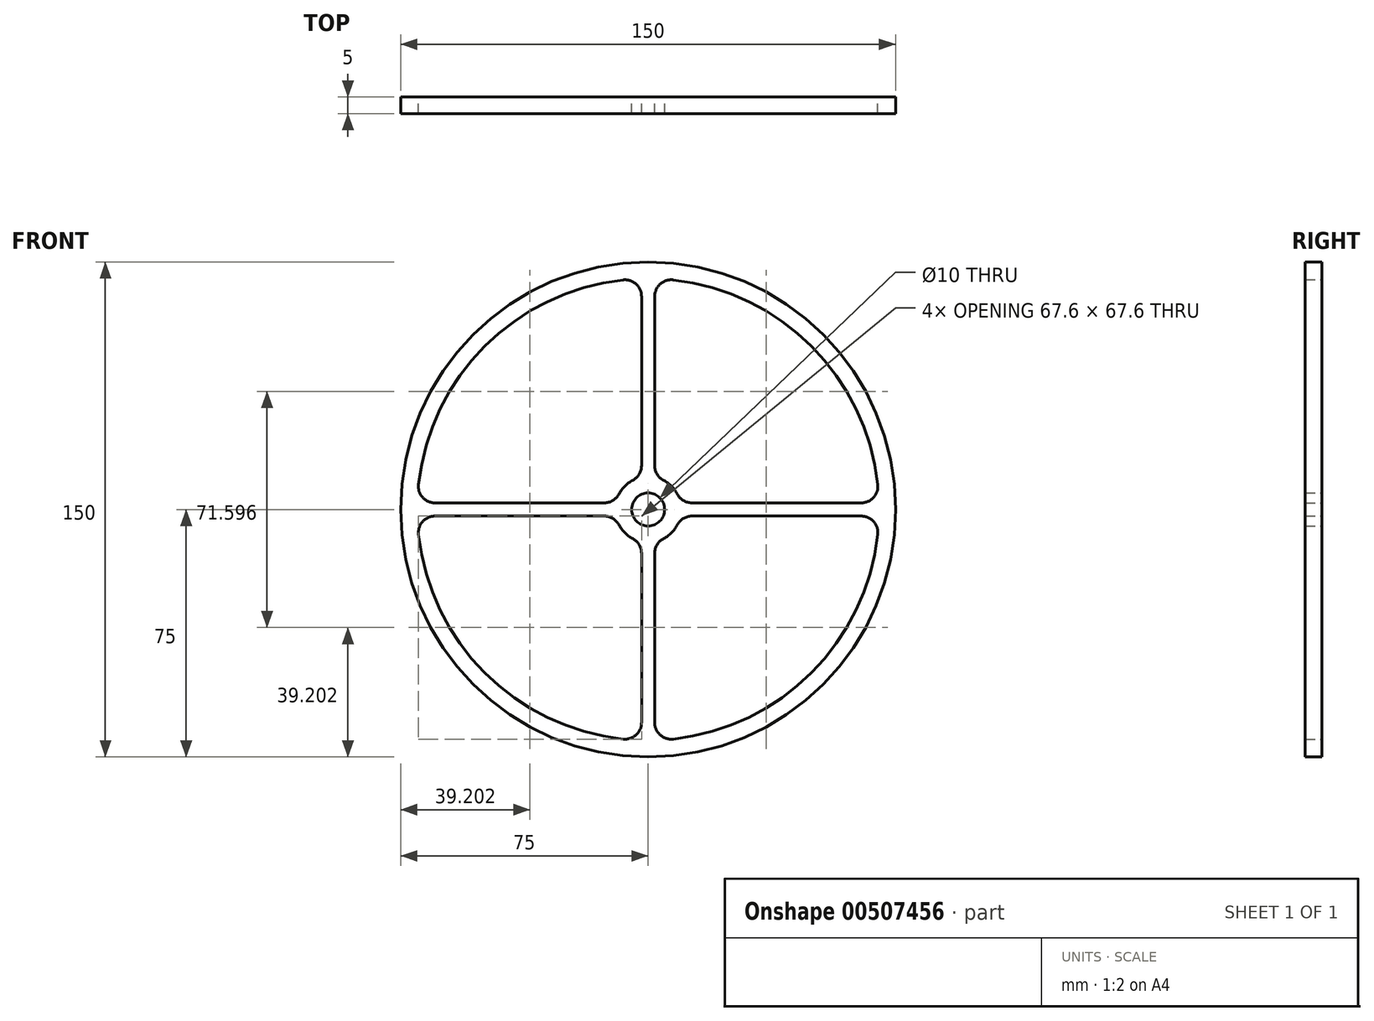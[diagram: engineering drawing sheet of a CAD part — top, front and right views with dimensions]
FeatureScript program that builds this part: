
annotation { "Feature Type Name" : "Feature", "Feature Type Description" : "" }
export const myFeature = defineFeature(function(context is Context, id is Id, definition is map)
    precondition{}
    {
        {
            var Q0;
            Q0=qCreatedBy(makeId("Front.planeOp"),FACE);
            var sketch = newSketch(context, id + "F0", { "sketchPlane" : qUnion([Q0])});
            skCircle(sketch, "E0", {"center": v(0, 0) * mm, "radius": 75 * mm});
            skArc(sketch, "E1", {"start": v(69.6, 7.54) * mm, "mid": v(49.5, 49.5) * mm, "end": v(7.54, 69.6) * mm});
            skCircle(sketch, "E2", {"center": v(0, 0) * mm, "radius": 5 * mm});
            skArc(sketch, "E3", {"start": v(-4.67, 8.84) * mm, "mid": v(-7.07, 7.07) * mm, "end": v(-8.84, 4.67) * mm});
            skLineSegment(sketch, "E4.0", {"start": v(2, 75) * mm, "end": v(2, 74.97) * mm});
            skLineSegment(sketch, "E5.MirrorCS", {"start": v(-2, 75) * mm, "end": v(-2, 74.97) * mm});
            skLineSegment(sketch, "E6.trimOffspring", {"start": v(-2, 64.62) * mm, "end": v(-2, 13.27) * mm});
            skLineSegment(sketch, "E7.trimOffspring", {"start": v(2, 64.62) * mm, "end": v(2, 13.27) * mm});
            skPoint(sketch, "E8.orphan", {"position": v(-2, 5) * mm});
            skPoint(sketch, "E9.orphan", {"position": v(2, 5) * mm});
            skPoint(sketch, "E10.start.orphan", {"position": v(0, 75) * mm});
            skLineSegment(sketch, "E11.1.0", {"start": v(-64.62, -2) * mm, "end": v(-13.27, -2) * mm});
            skLineSegment(sketch, "E11.1.1", {"start": v(-64.62, 2) * mm, "end": v(-13.27, 2) * mm});
            skLineSegment(sketch, "E11.2.0", {"start": v(2, -64.62) * mm, "end": v(2, -13.27) * mm});
            skLineSegment(sketch, "E11.2.1", {"start": v(-2, -64.62) * mm, "end": v(-2, -13.27) * mm});
            skLineSegment(sketch, "E11.3.0", {"start": v(64.62, 2) * mm, "end": v(13.27, 2) * mm});
            skLineSegment(sketch, "E11.3.1", {"start": v(64.62, -2) * mm, "end": v(13.27, -2) * mm});
            skArc(sketch, "E12.trimOffspring", {"start": v(-8.84, -4.67) * mm, "mid": v(-7.07, -7.07) * mm, "end": v(-4.67, -8.84) * mm});
            skArc(sketch, "E13.trimOffspring", {"start": v(8.84, 4.67) * mm, "mid": v(7.07, 7.07) * mm, "end": v(4.67, 8.84) * mm});
            skArc(sketch, "E14.trimOffspring", {"start": v(4.67, -8.84) * mm, "mid": v(7.07, -7.07) * mm, "end": v(8.84, -4.67) * mm});
            skArc(sketch, "E15.trimOffspring", {"start": v(-7.54, 69.6) * mm, "mid": v(-49.5, 49.5) * mm, "end": v(-69.6, 7.54) * mm});
            skArc(sketch, "E16.trimOffspring", {"start": v(-69.6, -7.54) * mm, "mid": v(-49.5, -49.5) * mm, "end": v(-7.54, -69.6) * mm});
            skArc(sketch, "E17.trimOffspring", {"start": v(7.54, -69.6) * mm, "mid": v(49.5, -49.5) * mm, "end": v(69.6, -7.54) * mm});
            skPoint(sketch, "E18.visualSharp", {"position": v(-2, 69.97) * mm});
            skArc(sketch, "E18.filletArc", {"start": v(-2, 64.62) * mm, "mid": v(-3.66, 68.34) * mm, "end": v(-7.54, 69.6) * mm});
            skPoint(sketch, "E19.visualSharp", {"position": v(2, 69.97) * mm});
            skArc(sketch, "E19.filletArc", {"start": v(7.54, 69.6) * mm, "mid": v(3.66, 68.34) * mm, "end": v(2, 64.62) * mm});
            skPoint(sketch, "E20.visualSharp", {"position": v(-69.97, 2) * mm});
            skArc(sketch, "E20.filletArc", {"start": v(-69.6, 7.54) * mm, "mid": v(-68.34, 3.66) * mm, "end": v(-64.62, 2) * mm});
            skPoint(sketch, "E21.visualSharp", {"position": v(-9.8, 2) * mm});
            skArc(sketch, "E21.filletArc", {"start": v(-13.27, 2) * mm, "mid": v(-10.68, 2.72) * mm, "end": v(-8.84, 4.67) * mm});
            skPoint(sketch, "E22.visualSharp", {"position": v(-2, 9.8) * mm});
            skArc(sketch, "E22.filletArc", {"start": v(-4.67, 8.84) * mm, "mid": v(-2.72, 10.68) * mm, "end": v(-2, 13.27) * mm});
            skPoint(sketch, "E23.visualSharp", {"position": v(2, 9.8) * mm});
            skArc(sketch, "E23.filletArc", {"start": v(2, 13.27) * mm, "mid": v(2.72, 10.68) * mm, "end": v(4.67, 8.84) * mm});
            skPoint(sketch, "E24.visualSharp", {"position": v(69.97, 2) * mm});
            skArc(sketch, "E24.filletArc", {"start": v(64.62, 2) * mm, "mid": v(68.34, 3.66) * mm, "end": v(69.6, 7.54) * mm});
            skPoint(sketch, "E25.visualSharp", {"position": v(9.8, -2) * mm});
            skArc(sketch, "E25.filletArc", {"start": v(13.27, -2) * mm, "mid": v(10.68, -2.72) * mm, "end": v(8.84, -4.67) * mm});
            skPoint(sketch, "E26.visualSharp", {"position": v(69.97, -2) * mm});
            skArc(sketch, "E26.filletArc", {"start": v(69.6, -7.54) * mm, "mid": v(68.34, -3.66) * mm, "end": v(64.62, -2) * mm});
            skPoint(sketch, "E27.visualSharp", {"position": v(2, -9.8) * mm});
            skArc(sketch, "E27.filletArc", {"start": v(4.67, -8.84) * mm, "mid": v(2.72, -10.68) * mm, "end": v(2, -13.27) * mm});
            skPoint(sketch, "E28.visualSharp", {"position": v(2, -69.97) * mm});
            skArc(sketch, "E28.filletArc", {"start": v(2, -64.62) * mm, "mid": v(3.66, -68.34) * mm, "end": v(7.54, -69.6) * mm});
            skPoint(sketch, "E29.visualSharp", {"position": v(-2, -9.8) * mm});
            skArc(sketch, "E29.filletArc", {"start": v(-2, -13.27) * mm, "mid": v(-2.72, -10.68) * mm, "end": v(-4.67, -8.84) * mm});
            skPoint(sketch, "E30.visualSharp", {"position": v(-9.8, -2) * mm});
            skArc(sketch, "E30.filletArc", {"start": v(-8.84, -4.67) * mm, "mid": v(-10.68, -2.72) * mm, "end": v(-13.27, -2) * mm});
            skPoint(sketch, "E31.visualSharp", {"position": v(-69.97, -2) * mm});
            skArc(sketch, "E31.filletArc", {"start": v(-64.62, -2) * mm, "mid": v(-68.34, -3.66) * mm, "end": v(-69.6, -7.54) * mm});
            skPoint(sketch, "E32.visualSharp", {"position": v(-2, -69.97) * mm});
            skArc(sketch, "E32.filletArc", {"start": v(-7.54, -69.6) * mm, "mid": v(-3.66, -68.34) * mm, "end": v(-2, -64.62) * mm});
            skPoint(sketch, "E33.visualSharp", {"position": v(9.8, 2) * mm});
            skArc(sketch, "E33.filletArc", {"start": v(8.84, 4.67) * mm, "mid": v(10.68, 2.72) * mm, "end": v(13.27, 2) * mm});
            skSolve(sketch);
        }
        {
            var Q0;
            Q0 = qSketchRegion(id + "F0", true);
            extrude(context, id + "F1", {"entities" : qUnion([Q0]), "endBound" : BoundingType.SYMMETRIC, "depth" : 5 * mm});
        }
    });
